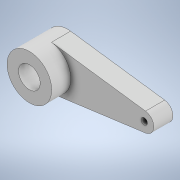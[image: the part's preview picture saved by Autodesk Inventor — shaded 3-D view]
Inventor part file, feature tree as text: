
AUTODESK INVENTOR PART (.ipt)
format: ipt  version: 2020 (Build 240168000, 168)  size: 122,880 bytes
history: native  units: mm
features: extrude x2, sketch x2, projected_geometry x1
ambient origin geometry x8: Origin, YZ Plane, XZ Plane, XY Plane, X Axis, Y Axis, Z Axis, Center Point
bodies: Solid1 (feature_tree)
feature tree (5):
  extrude  "Extrusion1"  Depth=7.0mm
  extrude  "Extrusion2"  Depth=3.0mm
  sketch  "Sketch1"  dims[d0=3.4mm d1=7.0mm]
  sketch  "Sketch2"  dims[d2=3.0mm d3=1.0mm d4=15.0mm d5=3.0mm d6=0.0mm d7=3.0mm d8=0.0mm]
  projected_geometry  "Projected Loop1"
